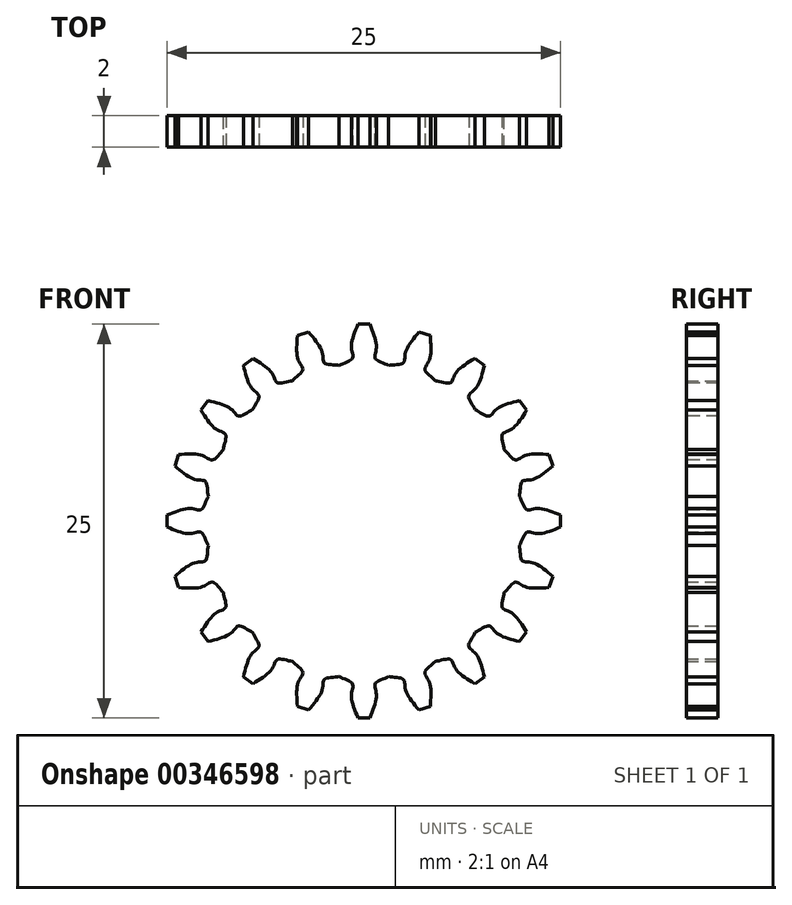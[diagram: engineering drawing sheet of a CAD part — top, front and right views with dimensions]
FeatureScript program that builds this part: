
annotation { "Feature Type Name" : "Feature", "Feature Type Description" : "" }
export const myFeature = defineFeature(function(context is Context, id is Id, definition is map)
    precondition{}
    {
        {
            var Q0;
            Q0=qCreatedBy(makeId("Front.planeOp"),FACE);
            var sketch = newSketch(context, id + "F0", { "sketchPlane" : qUnion([Q0])});
            skCircle(sketch, "E0", {"center": v(0, 0) * mm, "radius": 10 * mm});
            skSolve(sketch);
        }
        {
            var Q0;
            Q0=makeQuery(id+"F0.imprint","IMPRINT",FACE,{"disambiguationData":[TD([[makeQuery(id+"F0.imprint","IMPRINT",EDGE,{"derivedFrom":sQuery(id+"F0.wireOp",EDGE,"E0")}),1.0]])]});
            extrude(context, id + "F1", {"entities" : qUnion([Q0]), "depth" : 2 * mm});
        }
        {
            var Q0;
            Q0=qCreatedBy(makeId("Front.planeOp"),FACE);
            var sketch = newSketch(context, id + "F2", { "sketchPlane" : qUnion([Q0])});
            skArc(sketch, "E1.0", {"start": v(-1.56, -9.88) * mm, "mid": v(0, -10) * mm, "end": v(1.56, -9.88) * mm});
            skLineSegment(sketch, "E2", {"start": v(0, 0) * mm, "end": v(-1.56, -9.88) * mm, "construction": true});
            skLineSegment(sketch, "E3", {"start": v(0, 0) * mm, "end": v(1.56, -9.88) * mm, "construction": true});
            skLineSegment(sketch, "E4", {"start": v(-0.38, -12.5) * mm, "end": v(0.38, -12.5) * mm});
            skPoint(sketch, "E5", {"position": v(0, -12.5) * mm});
            skFitSpline(sketch, "E6", {"points": [v(-1.56, -9.88) * mm, v(-0.73, -10.32) * mm, v(-0.8, -10.95) * mm, v(-0.37, -12.5) * mm], "startDerivative": vector(2.03, -1.32) * mm, "endDerivative": vector(1.72, -4.17) * mm});
            skFitSpline(sketch, "E7.MirrorCS", {"points": [v(1.56, -9.88) * mm, v(0.73, -10.32) * mm, v(0.8, -10.95) * mm, v(0.37, -12.5) * mm], "startDerivative": vector(-2.03, -1.32) * mm, "endDerivative": vector(-1.72, -4.17) * mm});
            skSolve(sketch);
        }
        {
            var Q0;
            Q0 = qSketchRegion(id + "F2", true);
            extrude(context, id + "F3", {"entities" : qUnion([Q0]), "depth" : 2 * mm});
        }
        {
            var Q0;
            Q0=qCreatedBy(makeId("Top.planeOp"),FACE);
            var sketch = newSketch(context, id + "F4", { "sketchPlane" : qUnion([Q0])});
            skLineSegment(sketch, "E8", {"start": v(0, 24.93) * mm, "end": v(0, -36.4) * mm, "construction": true});
            skSolve(sketch);
        }
        {
            var Q0;
            Q0=makeQuery(id+"F3.opExtrude","SWEPT_BODY",BODY,{"disambiguationData":[OSD([sQuery(id+"F2.wireOp",EDGE,"E1.0"),sQuery(id+"F2.wireOp",EDGE,"E4"),sQuery(id+"F2.wireOp",EDGE,"E6"),sQuery(id+"F2.wireOp",EDGE,"E7.MirrorCS")])]});
            var Q1;
            Q1=sQuery(id+"F4.wireOp",EDGE,"E8");
            circularPattern(context, id + "F5", {"operationType" : NewBodyOperationType.ADD, "entities" : qUnion([Q0]), "axis" : qUnion([Q1]), "angle" : 360 * degree, "instanceCount" : 20, "equalSpace" : true});
        }
    });
